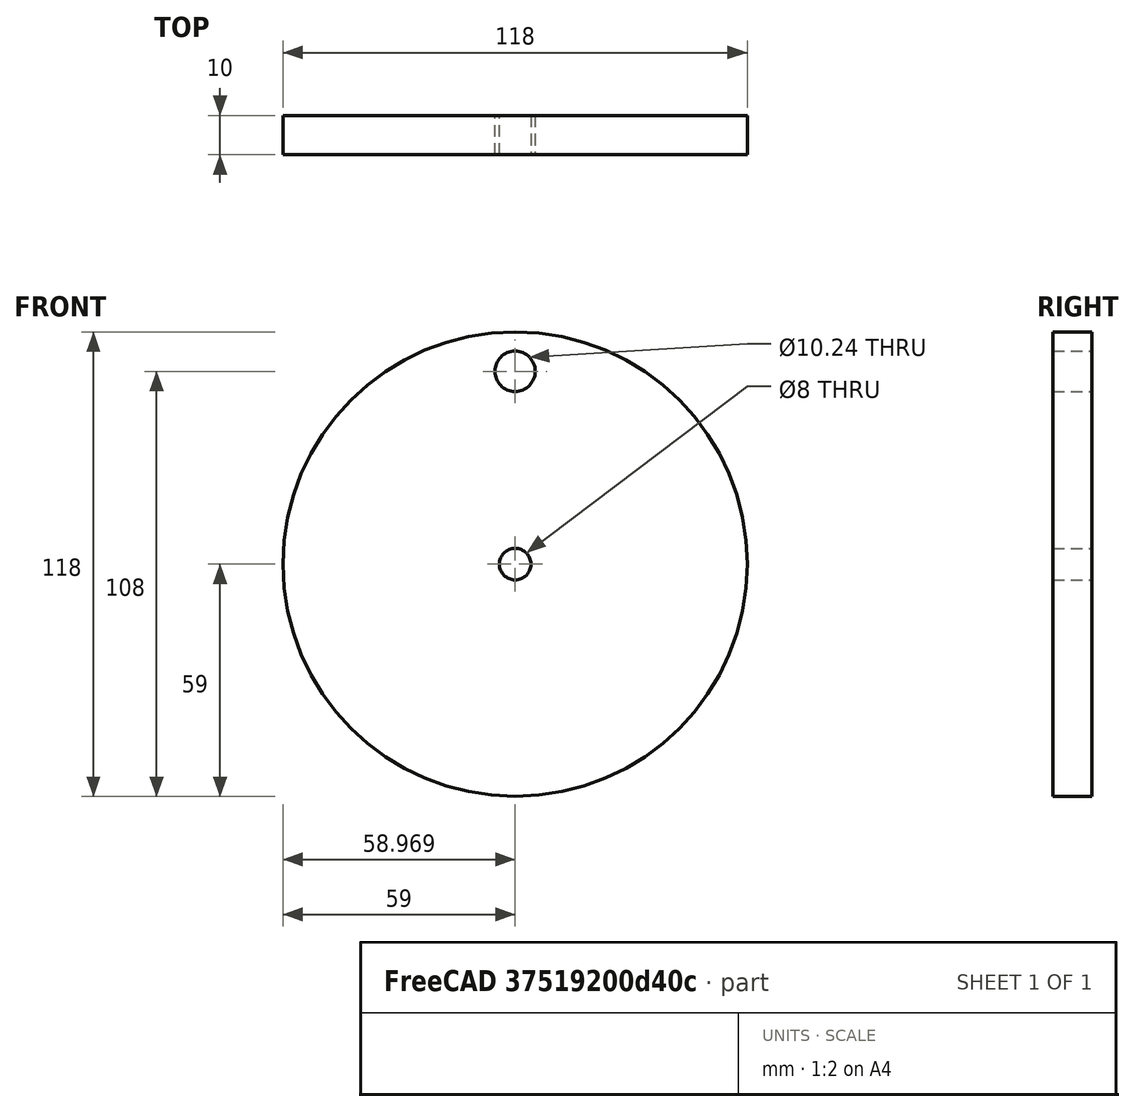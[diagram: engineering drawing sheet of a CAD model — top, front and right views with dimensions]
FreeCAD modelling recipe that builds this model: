
FCSTD DOCUMENT  (FreeCAD 0.18R4 (GitTag))
Label: manivel
License: All rights reserved
LicenseURL: http://en.wikipedia.org/wiki/All_rights_reserved
objects: App::FeaturePython×4, Drawing::FeatureViewPython×4, Drawing::FeatureViewPart×3, App::DocumentObjectGroup×2, Drawing::FeaturePage×2, Part::Feature×2, Sketcher::SketchObject×1, PartDesign::Pad×1, PartDesign::Body×1, Mesh::Feature×1
note: 6 computed .brp shape members not serialized (recipe doc carries the construction recipe); baked Part::Feature solids carry a one-line shape summary decoded from their .brp

FEATURE [Sketcher::SketchObject] Sketch
  MapMode = 5
  Placement = pos=(0,0,0) rot=(1,0,0;1.5708rad)
  Support = -> [XZ_Plane]
  sketch-geometry (7):
    g0: GeomPoint X=-59 Y=0.087979 Z=0
    g1: Circle CenterX=0 CenterY=0 CenterZ=0 NormalX=0 NormalY=0 NormalZ=1 AngleXU=0 Radius=59.0001
    g2: GeomPoint X=4 Y=-0.003993 Z=0
    g3: Circle CenterX=0 CenterY=0 CenterZ=0 NormalX=0 NormalY=0 NormalZ=1 AngleXU=0 Radius=4
    g4: GeomPoint X=-0.031242 Y=49 Z=0
    g5: GeomPoint X=-0.007981 Y=54 Z=0
    g6: Circle CenterX=-0.031242 CenterY=49 CenterZ=0 NormalX=0 NormalY=0 NormalZ=1 AngleXU=0 Radius=5.11824
  constraints (4):
    c: DistanceX(g0,g-1) = 59
    c: DistanceX(g1,g2) = 4
    c: DistanceY(g1,g4) = 49
    c: DistanceY(g4,g5) = 5
FEATURE [PartDesign::Pad] Pad
  Length = 10
  Length2 = 100
  Placement = pos=(0,0,0) rot=(1,0,0;1.5708rad)
  Profile = -> Sketch
  Type = 0
FEATURE [PartDesign::Body] Body
  Group = -> [Sketch,Pad]
  Origin = -> Origin
  Tip = -> Pad
FEATURE [App::FeaturePython] Dimension  # Draft dimension (typed FeaturePython)
  Diameter = true
  Dimline = (53.3589,-10,-25.0579)
  Direction = (0,0,0)
  Distance = 118
  End = (53.4045,-10,-25.0793)
  LinkedGeometry = -> [Pad]
  Normal = (0,0,-1)
  Start = (-53.4045,-10,25.0793)
  Support = -> Pad
FEATURE [App::FeaturePython] Dimension001  # Draft dimension (typed FeaturePython)
  Diameter = false
  Dimline = (66.4513,-0.403256,0)
  Direction = (0,0,0)
  Distance = 10.0002
  End = (58.9985,-3.5463e-09,0.0297485)
  Normal = (0,0,-1)
  Start = (58.9987,-10,-0.0258045)
FEATURE [App::FeaturePython] Dimension002  # Draft dimension (typed FeaturePython)
  Diameter = true
  Dimline = (3.05602,-10,2.5627)
  Direction = (0,0,0)
  Distance = 8
  End = (3.06497,-10,2.57021)
  LinkedGeometry = -> [Pad]
  Normal = (0,0,-1)
  Start = (-3.06497,-10,-2.57021)
  Support = -> Pad
FEATURE [App::FeaturePython] Dimension003  # Draft dimension (typed FeaturePython)
  Diameter = true
  Dimline = (4.93827,-10,50.2249)
  Direction = (0,0,0)
  Distance = 10.2365
  End = (4.93827,-10,50.2249)
  LinkedGeometry = -> [Pad]
  Normal = (0,0,-1)
  Start = (-5.00075,-10,47.7751)
  Support = -> Pad
FEATURE [App::DocumentObjectGroup] Grupo  label="Grupo1"
  Group = -> [Dimension003,Dimension002,Dimension]
FEATURE [App::DocumentObjectGroup] Grupo001  label="Grupo2"
  Group = -> [Dimension001]
FEATURE [Drawing::FeatureViewPart] Ortho  label="Ortho_0_0"
  Direction = (1,0,0)
  HiddenWidth = 0.15
  LineWidth = 0.35
  Rotation = -90
  Scale = 0.5
  ShowHiddenLines = false
  ShowSmoothLines = false
  Source = -> Body
  Tolerance = 0.05
  ViewResult = <g id="Ortho_0_0"\n   transform="rotate(-90,161.333,72.5) translate(161.333,72.5) scale(0.5,0.5)"\n  >\n<g   fill="none"\n   stroke="rgb(0, 0, 0)"\n   stroke-linecap="butt"\n   stroke-linejoin="miter"\n   stroke-width="0.700000"\n   transform="scale(1,-1)"\n  >\n<path id= "1" d=" M -59.0001 10 L -59.0001 3.90607e-14 " />\n<path id= "2" d=" M 59.0001 10 L 59.0001 -3.90607e-14 " />\n</g>\n<g   fill="none"\n   stroke="rgb(0, 0, 0)"\n   stroke-linecap="butt"\n   stroke-linejoin="miter"\n   stroke-width="0.700000"\n   transform="scale(1,-1)"\n  >\n<path d="M0,0 L6.60591,-1.46681e-15  L13.1287,-2.91517e-15  L19.4865,-4.32687e-15  L25.5992,-5.68416e-15  L31.3899,-6.96996e-15  L36.7859,-8.16812e-15  L41.7193,-9.26356e-15  L46.1281,-1.02425e-14  L49.9568,-1.10926e-14  L53.1572,-1.18033e-14  L55.6892,-1.23655e-14  L57.5208,-1.27722e-14  L58.6291,-1.30183e-14  L59.0001,-1.31006e-14 " /><path d="M-59.0001,1.31006e-14 L-58.6291,1.30183e-14  L-57.5208,1.27722e-14  L-55.6892,1.23655e-14  L-53.1572,1.18033e-14  L-49.9568,1.10926e-14  L-46.1281,1.02425e-14  L-41.7193,9.26356e-15  L-36.7859,8.16812e-15  L-31.3899,6.96996e-15  L-25.5992,5.68416e-15  L-19.4865,4.32687e-15  L-13.1287,2.91517e-15  L-6.60591,1.46681e-15  L-1.46549e-14,3.25405e-30 " /><path d="M7.10543e-15,10 L6.60591,10  L13.1287,10  L19.4865,10  L25.5992,10  L31.3899,10  L36.7859,10  L41.7193,10  L46.1281,10  L49.9568,10  L53.1572,10  L55.6892,10  L57.5208,10  L58.6291,10  L59.0001,10 " /><path d="M-59.0001,10 L-58.6291,10  L-57.5208,10  L-55.6892,10  L-53.1572,10  L-49.9568,10  L-46.1281,10  L-41.7193,10  L-36.7859,10  L-31.3899,10  L-25.5992,10  L-19.4865,10  L-13.1287,10  L-6.60591,10  L-7.10543e-15,10 " /></g>\n</g>
  Visible = true
  X = 161.333
  Y = 72.5
FEATURE [Drawing::FeatureViewPart] Ortho001  label="Ortho_-1_0"
  Direction = (0,-1,0)
  HiddenWidth = 0.15
  LineWidth = 0.35
  Rotation = 90
  Scale = 0.5
  ShowHiddenLines = false
  ShowSmoothLines = false
  Source = -> Body
  Tolerance = 0.05
  ViewResult = <g id="Ortho_-1_0"\n   transform="rotate(90,88.1667,72.5) translate(88.1667,72.5) scale(0.5,0.5)"\n  >\n<g   fill="none"\n   stroke="rgb(0, 0, 0)"\n   stroke-linecap="butt"\n   stroke-linejoin="miter"\n   stroke-width="0.700000"\n   transform="scale(1,-1)"\n  >\n<circle cx ="-7.10543e-15" cy ="0" r ="59.0001" /><circle cx ="-49" cy ="-0.031242" r ="5.11824" /><circle cx ="-7.10543e-15" cy ="0" r ="4" /></g>\n</g>
  Visible = true
  X = 88.1667
  Y = 72.5
FEATURE [Drawing::FeatureViewPart] Ortho002  label="Ortho_-1_-1"
  Direction = (0.57735,-0.57735,-0.57735)
  HiddenWidth = 0.15
  LineWidth = 0.35
  Rotation = 120
  Scale = 0.5
  ShowHiddenLines = false
  ShowSmoothLines = false
  Source = -> Body
  Tolerance = 0.05
  ViewResult = <g id="Ortho_-1_-1"\n   transform="rotate(120,89.9344,165.521) translate(89.9344,165.521) scale(0.5,0.5)"\n  >\n<g   fill="none"\n   stroke="rgb(0, 0, 0)"\n   stroke-linecap="butt"\n   stroke-linejoin="miter"\n   stroke-width="0.700000"\n   transform="scale(1,-1)"\n  >\n<path id= "1" d=" M 59.0001 -8.16497 L 59.0001 -3.19744e-14 " />\n<path id= "2" d=" M -59.0001 -8.16497 L -59.0001 3.19744e-14 " />\n</g>\n<g   fill="none"\n   stroke="rgb(0, 0, 0)"\n   stroke-linecap="butt"\n   stroke-linejoin="miter"\n   stroke-width="0.700000"\n   transform="scale(1,-1)"\n  >\n<path d="M-41.7193 24.0867 A59.0001 34.0637 180 0 1 -59.0001 1.83713e-14" />\n<path d="M59.0001 -1.41997e-14 A59.0001 34.0637 180 0 1 -41.7193 24.0867" />\n<path d="M-41.7193 15.9217 A59.0001 34.0637 180 0 1 -59.0001 -8.16497" />\n<path d="M-59.0001 -8.16497 A59.0001 34.0637 180 0 1 59.0001 -8.16497" />\n<path d="M59.0001 -8.16497 A59.0001 34.0637 180 0 1 -41.7193 15.9217" />\n<path d="M-38.2453 -26.0924 A5.11824 2.95501 180 0 1 -39.7444 -28.1819" />\n<path d="M-39.7444 -28.1819 A5.11824 2.95501 180 0 1 -29.5079 -28.1819" />\n<path d="M-29.5079 -28.1819 A5.11824 2.95501 180 0 1 -38.2453 -26.0924" />\n<path d="M-2.82843 -6.53197 A4 2.3094 180 0 1 -4 -8.16497" />\n<path d="M-4 -8.16497 A4 2.3094 180 0 1 4 -8.16497" />\n<path d="M4 -8.16497 A4 2.3094 180 0 1 -2.82843 -6.53197" />\n</g>\n</g>
  Visible = true
  X = 89.9344
  Y = 165.521
FEATURE [Drawing::FeatureViewPython] dim001  # drawing view (typed FeaturePython)
  Rotation = 0
  ViewResult = <g> \n  <line x1="156.333000" y1="41.185450" x2="156.333000" y2="32.290575" style="stroke:rgb(0,0,255);stroke-width:0.50" />\n<line x1="161.333000" y1="40.999950" x2="161.333000" y2="32.290575" style="stroke:rgb(0,0,255);stroke-width:0.50" />\n<line x1="156.333000" y1="33.290575" x2="161.333000" y2="33.290575" style="stroke:rgb(0,0,255);stroke-width:0.50" /> \n  <polygon points="161.333000,33.290575 164.333000,34.290575 165.333000,33.290575 164.333000,32.290575" style="fill:rgb(0,0,255);stroke:rgb(0,0,255);stroke-width:0" /><polygon points="156.333000,33.290575 153.333000,32.290575 152.333000,33.290575 153.333000,34.290575" style="fill:rgb(0,0,255);stroke:rgb(0,0,255);stroke-width:0" /> \n  <text x="158.833000" y="31.290575" font-family="inherit" font-size="3.6" fill="rgb(0,0,255)" text-anchor="middle" transform="rotate(0.000000 158.833000,31.290575)" >10</text> </g>
  Visible = true
  X = 0
  Y = 0
  arrowL1 = 3
  arrowL2 = 1
  arrowW = 2
  arrow_scheme = 0
  autoPlaceOffset = 2
  autoPlaceText = true
  click1_x = 158.79
  click1_y = 33.2906
  click2_x = 158.79
  click2_y = 33.2906
  comma_decimal_place = false
  dimension_line_overshoot = 1
  gap_datum_points = 2
  halfDimension_linear = false
  lineColor = rgb(0,0,255)
  strokeWidth = 0.5
  textFormat_linear = %(value)3.3f
  textRenderer_color = rgb(0,0,255)
  textRenderer_family = inherit
  textRenderer_size = 3.6
  unit_custom_scale = 1
  unit_scheme = 0
FEATURE [Drawing::FeatureViewPython] dim002  # drawing view (typed FeaturePython)
  Rotation = 0
  ViewResult = <g> \n  <line x1="117.666750" y1="70.500000" x2="117.666750" y2="28.521831" style="stroke:rgb(0,0,255);stroke-width:0.50" />\n<line x1="58.666650" y1="70.500000" x2="58.666650" y2="28.521831" style="stroke:rgb(0,0,255);stroke-width:0.50" />\n<line x1="117.666750" y1="29.521831" x2="58.666650" y2="29.521831" style="stroke:rgb(0,0,255);stroke-width:0.50" /> \n  <polygon points="58.666650,29.521831 61.666650,30.521831 62.666650,29.521831 61.666650,28.521831" style="fill:rgb(0,0,255);stroke:rgb(0,0,255);stroke-width:0" /><polygon points="117.666750,29.521831 114.666750,28.521831 113.666750,29.521831 114.666750,30.521831" style="fill:rgb(0,0,255);stroke:rgb(0,0,255);stroke-width:0" /> \n  <text x="88.166700" y="27.521831" font-family="inherit" font-size="3.6" fill="rgb(0,0,255)" text-anchor="middle" transform="rotate(0.000000 88.166700,27.521831)" >118</text> </g>
  Visible = true
  X = 0
  Y = 0
  arrowL1 = 3
  arrowL2 = 1
  arrowW = 2
  arrow_scheme = 0
  autoPlaceOffset = 2
  autoPlaceText = true
  click1_x = 66.4555
  click1_y = 29.5218
  click2_x = 66.4555
  click2_y = 29.5218
  comma_decimal_place = false
  dimension_line_overshoot = 1
  gap_datum_points = 2
  halfDimension_linear = false
  lineColor = rgb(0,0,255)
  strokeWidth = 0.5
  textFormat_linear = %(value)3.3f
  textRenderer_color = rgb(0,0,255)
  textRenderer_family = inherit
  textRenderer_size = 3.6
  unit_custom_scale = 1
  unit_scheme = 0
FEATURE [Drawing::FeatureViewPython] dim003  # drawing view (typed FeaturePython)
  Rotation = 0
  ViewResult = <g> \n  <line x1="163.333000" y1="102.000050" x2="167.034126" y2="102.000050" style="stroke:rgb(0,0,255);stroke-width:0.50" />\n<line x1="163.333000" y1="42.999950" x2="167.034126" y2="42.999950" style="stroke:rgb(0,0,255);stroke-width:0.50" />\n<line x1="166.034126" y1="102.000050" x2="166.034126" y2="42.999950" style="stroke:rgb(0,0,255);stroke-width:0.50" /> \n  <polygon points="166.034126,42.999950 165.034126,45.999950 166.034126,46.999950 167.034126,45.999950" style="fill:rgb(0,0,255);stroke:rgb(0,0,255);stroke-width:0" /><polygon points="166.034126,102.000050 167.034126,99.000050 166.034126,98.000050 165.034126,99.000050" style="fill:rgb(0,0,255);stroke:rgb(0,0,255);stroke-width:0" /> \n  <text x="164.034126" y="72.500000" font-family="inherit" font-size="3.6" fill="rgb(0,0,255)" text-anchor="middle" transform="rotate(-90.000000 164.034126,72.500000)" >118</text> </g>
  Visible = true
  X = 0
  Y = 0
  arrowL1 = 3
  arrowL2 = 1
  arrowW = 2
  arrow_scheme = 0
  autoPlaceOffset = 2
  autoPlaceText = true
  click1_x = 166.034
  click1_y = 54.3327
  click2_x = 166.034
  click2_y = 54.3327
  comma_decimal_place = false
  dimension_line_overshoot = 1
  gap_datum_points = 2
  halfDimension_linear = false
  lineColor = rgb(0,0,255)
  strokeWidth = 0.5
  textFormat_linear = %(value)3.3f
  textRenderer_color = rgb(0,0,255)
  textRenderer_family = inherit
  textRenderer_size = 3.6
  unit_custom_scale = 1
  unit_scheme = 0
FEATURE [Drawing::FeatureViewPython] dim004  # drawing view (typed FeaturePython)
  Rotation = 0
  ViewResult = <g> \n  <line x1="90.166700" y1="74.500000" x2="90.166700" y2="109.142026" style="stroke:rgb(0,0,255);stroke-width:0.50" />\n<line x1="86.166700" y1="74.500000" x2="86.166700" y2="109.142026" style="stroke:rgb(0,0,255);stroke-width:0.50" />\n<line x1="90.166700" y1="108.142026" x2="86.166700" y2="108.142026" style="stroke:rgb(0,0,255);stroke-width:0.50" /> \n  <polygon points="86.166700,108.142026 83.166700,107.142026 82.166700,108.142026 83.166700,109.142026" style="fill:rgb(0,0,255);stroke:rgb(0,0,255);stroke-width:0" /><polygon points="90.166700,108.142026 93.166700,109.142026 94.166700,108.142026 93.166700,107.142026" style="fill:rgb(0,0,255);stroke:rgb(0,0,255);stroke-width:0" /> \n  <text x="88.166700" y="106.142026" font-family="inherit" font-size="3.6" fill="rgb(0,0,255)" text-anchor="middle" transform="rotate(0.000000 88.166700,106.142026)" >8</text> </g>
  Visible = true
  X = 0
  Y = 0
  arrowL1 = 3
  arrowL2 = 1
  arrowW = 2
  arrow_scheme = 0
  autoPlaceOffset = 2
  autoPlaceText = true
  click1_x = 88.3561
  click1_y = 108.142
  click2_x = 88.3561
  click2_y = 108.142
  comma_decimal_place = false
  dimension_line_overshoot = 1
  gap_datum_points = 2
  halfDimension_linear = false
  lineColor = rgb(0,0,255)
  strokeWidth = 0.5
  textFormat_linear = %(value)3.3f
  textRenderer_color = rgb(0,0,255)
  textRenderer_family = inherit
  textRenderer_size = 3.6
  unit_custom_scale = 1
  unit_scheme = 0
FEATURE [Drawing::FeaturePage] Page001
  EditableTexts = AUTHOR NAME | DRAWING TITLE | FreeCAD DRAWING | A4 | X / Y | SCALE | PN | DN | DD/MM/YYYY | REV A
  Group = -> [Ortho,Ortho001,Ortho002,dim001,dim002,dim003,dim004]
  Template = <path>
FEATURE [Mesh::Feature] Sin_t__tulo__4_  label="Sin título (4)"
FEATURE [Part::Feature] Sin_t__tulo__4_001
  shape: bbox 191.2 x 60.21 x 100.2 mm, 1624 faces, 0 solids (baked)
FEATURE [Part::Feature] Sin_t__tulo__4_001_solid  label="Sin_t__tulo__4_001 (Solid)"
  shape: bbox 191.2 x 60.21 x 100.2 mm, 1624 faces (baked)
FEATURE [Drawing::FeaturePage] Page
  EditableTexts = AUTHOR NAME | DRAWING TITLE | FreeCAD DRAWING | A4 | X / Y | SCALE | PN | DN | DD/MM/YYYY | REV A
  Template = <path>
note: 2 file-system paths scrubbed to <path> (originals preserved in the JSON sidecar)
